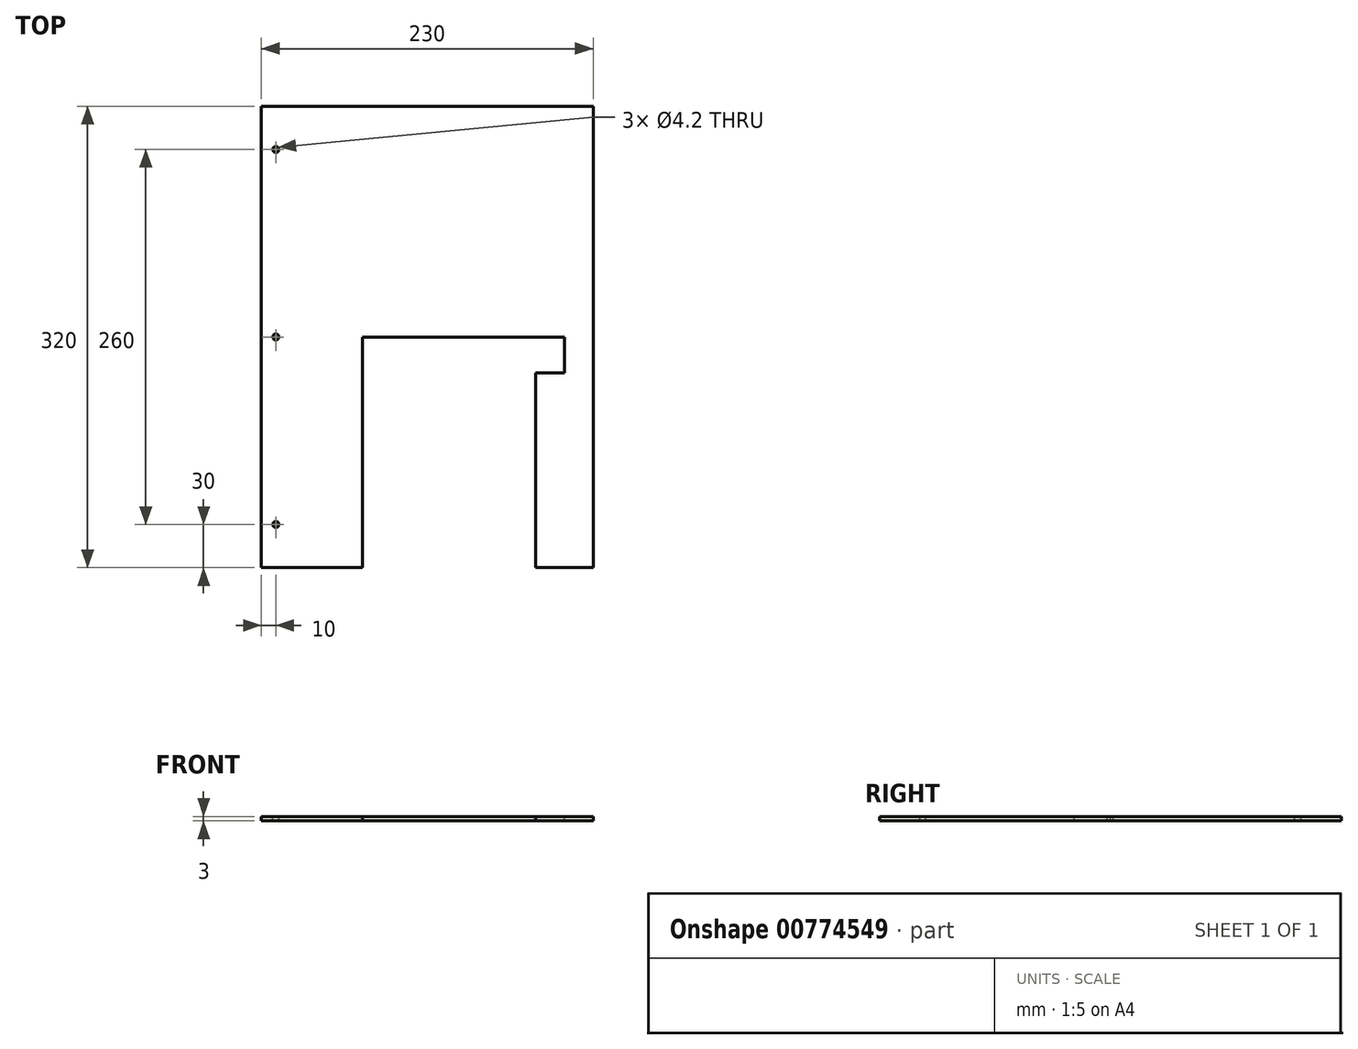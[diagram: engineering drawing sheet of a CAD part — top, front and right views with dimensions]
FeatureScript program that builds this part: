
annotation { "Feature Type Name" : "Feature", "Feature Type Description" : "" }
export const myFeature = defineFeature(function(context is Context, id is Id, definition is map)
    precondition{}
    {
        {
            assignVariable(context, id + "F0", {"name" : "Epaisseur", "anyValue" : 3});
        }
        {
            var Q0;
            Q0=qCreatedBy(makeId("Top.planeOp"),FACE);
            var sketch = newSketch(context, id + "F1", { "sketchPlane" : qUnion([Q0])});
            skLineSegment(sketch, "E0.bottom", {"start": v(-115, -160) * mm, "end": v(115, -160) * mm});
            skLineSegment(sketch, "E0.top", {"start": v(-115, 160) * mm, "end": v(115, 160) * mm});
            skLineSegment(sketch, "E0.left", {"start": v(-115, -160) * mm, "end": v(-115, 160) * mm});
            skLineSegment(sketch, "E0.right", {"start": v(115, -160) * mm, "end": v(115, 160) * mm});
            skPoint(sketch, "E0.middle", {"position": v(0, 0) * mm});
            skSolve(sketch);
        }
        {
            var Q0;
            Q0=makeQuery(id+"F1.imprint","IMPRINT",FACE,{"disambiguationData":[TD([[makeQuery(id+"F1.imprint","IMPRINT",EDGE,{"derivedFrom":sQuery(id+"F1.wireOp",EDGE,"E0.bottom")}),1.0]])]});
            extrude(context, id + "F2", {"entities" : qUnion([Q0]), "depth" : (getVariable(context, 'Epaisseur')) * mm, "offsetDistance" : 25 * mm});
        }
        {
            var Q0;
            Q0=makeQuery(id+"F2.opExtrude","CAP_FACE",FACE,{"disambiguationData":[OSD([sQuery(id+"F1.wireOp",EDGE,"E0.bottom"),sQuery(id+"F1.wireOp",EDGE,"E0.top"),sQuery(id+"F1.wireOp",EDGE,"E0.left"),sQuery(id+"F1.wireOp",EDGE,"E0.right")])],"isStart":false});
            var sketch = newSketch(context, id + "F3", { "sketchPlane" : qUnion([Q0])});
            skLineSegment(sketch, "E1", {"start": v(-105, 160) * mm, "end": v(-105, -160) * mm, "construction": true});
            skPoint(sketch, "E2", {"position": v(-105, 130) * mm});
            skPoint(sketch, "E3", {"position": v(-105, 0) * mm});
            skPoint(sketch, "E4", {"position": v(-105, -130) * mm});
            skSolve(sketch);
        }
        {
            var Q0;
            Q0=sQuery(id+"F3.wireOp",VERTEX,"E2");
            var Q1;
            Q1=sQuery(id+"F3.wireOp",VERTEX,"E3");
            var Q2;
            Q2=sQuery(id+"F3.wireOp",VERTEX,"E4");
            var Q3;
            Q3=makeQuery(id+"F2.opExtrude","SWEPT_BODY",BODY,{"disambiguationData":[OSD([sQuery(id+"F1.wireOp",EDGE,"E0.bottom"),sQuery(id+"F1.wireOp",EDGE,"E0.top"),sQuery(id+"F1.wireOp",EDGE,"E0.left"),sQuery(id+"F1.wireOp",EDGE,"E0.right")])]});
            hole(context, id + "F4", {"style" : HoleStyle.SIMPLE, "endStyle" : HoleEndStyle.BLIND, "holeDiameter" : 4.2 * mm, "majorDiameter" : 5 * mm, "holeDepth" : 4 * mm, "isTappedThrough" : true, "tappedDepth" : 2.3 * mm, "tapClearance" : 3, "startFromSketch" : true, "locations" : qUnion([Q0, Q1, Q2]), "scope" : qUnion([Q3])});
        }
        {
            var Q0;
            Q0=makeQuery(id+"F2.opExtrude","CAP_FACE",FACE,{"disambiguationData":[OSD([sQuery(id+"F1.wireOp",EDGE,"E0.bottom"),sQuery(id+"F1.wireOp",EDGE,"E0.top"),sQuery(id+"F1.wireOp",EDGE,"E0.left"),sQuery(id+"F1.wireOp",EDGE,"E0.right")])],"isStart":false});
            var sketch = newSketch(context, id + "F5", { "sketchPlane" : qUnion([Q0])});
            skLineSegment(sketch, "E5.bottom", {"start": v(-45, -160) * mm, "end": v(75, -160) * mm});
            skLineSegment(sketch, "E5.top", {"start": v(-45, 0) * mm, "end": v(75, 0) * mm});
            skLineSegment(sketch, "E5.left", {"start": v(-45, -160) * mm, "end": v(-45, 0) * mm});
            skLineSegment(sketch, "E5.right", {"start": v(75, -160) * mm, "end": v(75, 0) * mm});
            skPoint(sketch, "E5.middle", {"position": v(15, -80) * mm});
            skSolve(sketch);
        }
        {
            var Q0;
            Q0=makeQuery(id+"F5.imprint","IMPRINT",FACE,{"disambiguationData":[TD([[makeQuery(id+"F5.imprint","IMPRINT",EDGE,{"derivedFrom":sQuery(id+"F5.wireOp",EDGE,"E5.bottom")}),1.0]])]});
            extrude(context, id + "F6", {"entities" : qUnion([Q0]), "operationType" : NewBodyOperationType.REMOVE, "oppositeDirection" : true, "depth" : 25 * mm, "offsetDistance" : 25 * mm});
        }
        {
            var Q0;
            Q0=makeQuery(id+"F2.opExtrude","CAP_FACE",FACE,{"disambiguationData":[OSD([sQuery(id+"F1.wireOp",EDGE,"E0.bottom"),sQuery(id+"F1.wireOp",EDGE,"E0.top"),sQuery(id+"F1.wireOp",EDGE,"E0.left"),sQuery(id+"F1.wireOp",EDGE,"E0.right")])],"isStart":false});
            var sketch = newSketch(context, id + "F7", { "sketchPlane" : qUnion([Q0])});
            skLineSegment(sketch, "E6.bottom", {"start": v(75, 0) * mm, "end": v(95, 0) * mm});
            skLineSegment(sketch, "E6.top", {"start": v(75, -25) * mm, "end": v(95, -25) * mm});
            skLineSegment(sketch, "E6.left", {"start": v(75, 0) * mm, "end": v(75, -25) * mm});
            skLineSegment(sketch, "E6.right", {"start": v(95, 0) * mm, "end": v(95, -25) * mm});
            skSolve(sketch);
        }
        {
            var Q0;
            Q0=makeQuery(id+"F7.imprint","IMPRINT",FACE,{"disambiguationData":[TD([[makeQuery(id+"F7.imprint","IMPRINT",EDGE,{"derivedFrom":sQuery(id+"F7.wireOp",EDGE,"E6.bottom")}),-1.0]])]});
            extrude(context, id + "F8", {"entities" : qUnion([Q0]), "operationType" : NewBodyOperationType.REMOVE, "endBound" : BoundingType.UP_TO_NEXT, "oppositeDirection" : true, "depth" : 25 * mm, "offsetDistance" : 25 * mm});
        }
    });
